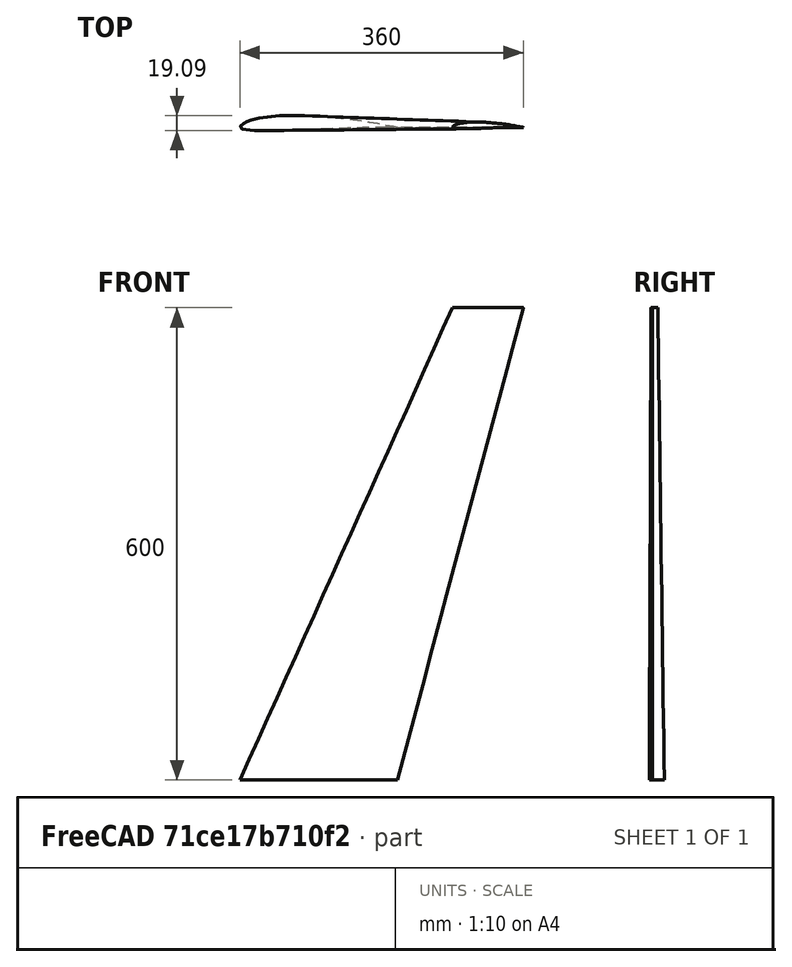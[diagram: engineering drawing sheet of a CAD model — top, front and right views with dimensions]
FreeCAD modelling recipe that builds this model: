
FCSTD DOCUMENT  (FreeCAD 1.0R39109 (Git))
Label: SD7037 Airfoil Wing 160cm Wingspan
License: All rights reserved
LicenseURL: https://en.wikipedia.org/wiki/All_rights_reserved
objects: Part::Part2DObjectPython×4, Sketcher::SketchObject×4, App::DocumentObjectGroup×1, PartDesign::AdditiveLoft×1, PartDesign::Body×1
note: 16 computed .brp shape members not serialized (recipe doc carries the construction recipe); baked Part::Feature solids carry a one-line shape summary decoded from their .brp

FEATURE [Part::Part2DObjectPython] Wire  # Draft 2D object (typed FeaturePython)
  Area = 0.0605284
  ChamferSize = 0
  Closed = true
  End = (1,0,0)
  FilletRadius = 0
  Length = 2.02979
  MakeFace = true
  Points = (61) [(1,0,0),(0.99672,0.00042,0),(0.98707,0.0018,0),(0.97146,0.00436,0),(0.95041,0.00811,0),(0.9245,0.01295,0),(0.89425,0.01865,0),(0.86015,0.0249,0),+53 more]
  Start = (1,0,0)
  Subdivisions = 0
FEATURE [App::DocumentObjectGroup] sd7037
  Group = -> [Wire]
FEATURE [Part::Part2DObjectPython] BSpline  label="SD7037 20CM Length"  # Draft 2D object (typed FeaturePython)
  Area = 2428.78
  Closed = true
  MakeFace = true
  Parameterization = 1
  Points = (60) [(200,0,0),(199.344,0.084,0),(197.414,0.36,0),(194.292,0.872,0),(190.082,1.622,0),(184.9,2.59,0),(178.85,3.73,0),(172.03,4.98,0),(164.522,6.282,0),+51 more]
FEATURE [Part::Part2DObjectPython] BSpline001  label="Original SD7038"  # Draft 2D object (typed FeaturePython)
  Area = 0.0607194
  Closed = true
  MakeFace = true
  Parameterization = 1
  Points = (60) [(1,0,0),(0.99672,0.00042,0),(0.98707,0.0018,0),(0.97146,0.00436,0),(0.95041,0.00811,0),(0.9245,0.01295,0),(0.89425,0.01865,0),(0.86015,0.0249,0),+52 more]
FEATURE [Part::Part2DObjectPython] BSpline002  label="SD7039 9CM Length"  # Draft 2D object (typed FeaturePython)
  Area = 491.827
  Closed = true
  MakeFace = true
  Parameterization = 1
  Points = (60) [(90,0,0),(89.7048,0.0378,0),(88.8363,0.162,0),(87.4314,0.3924,0),(85.5369,0.7299,0),(83.205,1.1655,0),(80.4825,1.6785,0),(77.4135,2.241,0),+52 more]
FEATURE [Sketcher::SketchObject] Sketch
  ArcFitTolerance = 1e-06
  FullyConstrained = false
  MakeInternals = false
  sketch-geometry (123):
    g0: BSplineCurve PolesCount=61 KnotsCount=61 Degree=3 IsPeriodic=1
    g1-g61: Circle [constr] x61 (B-spline internal-alignment scaffolding for g0; pole/knot coordinates omitted)
    g62-g122: GeomPoint [constr] x61 (B-spline internal-alignment scaffolding for g0; pole/knot coordinates omitted)
  constraints (123):
    c: InternalAlignment(g1,g0)
    c: Weight(g1) = 1
    c: InternalAlignment(g2,g0)
    c: Equal(g2,g1)
    c: InternalAlignment(g3,g0)
    c: Equal(g3,g1)
    c: InternalAlignment(g4,g0)
    c: Equal(g4,g1)
    c: InternalAlignment(g5,g0)
    c: Equal(g5,g1)
    c: InternalAlignment(g6,g0)
    c: Equal(g6,g1)
    c: InternalAlignment(g7,g0)
    c: Equal(g7,g1)
    c: InternalAlignment(g8,g0)
    c: Equal(g8,g1)
    c: InternalAlignment(g9,g0)
    c: Equal(g9,g1)
    c: InternalAlignment(g10,g0)
    c: Equal(g10,g1)
    c: InternalAlignment(g11,g0)
    c: Equal(g11,g1)
    c: InternalAlignment(g12,g0)
    c: Equal(g12,g1)
    c: InternalAlignment(g13,g0)
    c: Equal(g13,g1)
    c: InternalAlignment(g14,g0)
    c: Equal(g14,g1)
    c: InternalAlignment(g15,g0)
    c: Equal(g15,g1)
    c: InternalAlignment(g16,g0)
    c: Equal(g16,g1)
    c: InternalAlignment(g17,g0)
    c: Equal(g17,g1)
    c: InternalAlignment(g18,g0)
    c: Equal(g18,g1)
    c: InternalAlignment(g19,g0)
    c: Equal(g19,g1)
    c: InternalAlignment(g20,g0)
    c: Equal(g20,g1)
    c: InternalAlignment(g21,g0)
    c: Equal(g21,g1)
    c: InternalAlignment(g22,g0)
    c: Equal(g22,g1)
    c: InternalAlignment(g23,g0)
    c: Equal(g23,g1)
    c: InternalAlignment(g24,g0)
    c: Equal(g24,g1)
    c: InternalAlignment(g25,g0)
    c: Equal(g25,g1)
    c: InternalAlignment(g26,g0)
    c: Equal(g26,g1)
    c: InternalAlignment(g27,g0)
    c: Equal(g27,g1)
    c: InternalAlignment(g28,g0)
    c: Equal(g28,g1)
    c: InternalAlignment(g29,g0)
    c: Equal(g29,g1)
    c: InternalAlignment(g30,g0)
    c: Equal(g30,g1)
    c: InternalAlignment(g31,g0)
    c: Equal(g31,g1)
    c: InternalAlignment(g32,g0)
    c: Equal(g32,g1)
    c: InternalAlignment(g33,g0)
    c: Equal(g33,g1)
    c: InternalAlignment(g34,g0)
    c: Equal(g34,g1)
    c: InternalAlignment(g35,g0)
    c: Equal(g35,g1)
    c: InternalAlignment(g36,g0)
    c: Equal(g36,g1)
    c: InternalAlignment(g37,g0)
    c: Equal(g37,g1)
    c: InternalAlignment(g38,g0)
    c: Equal(g38,g1)
    c: InternalAlignment(g39,g0)
    c: Equal(g39,g1)
    c: InternalAlignment(g40,g0)
    c: Equal(g40,g1)
    c: InternalAlignment(g41,g0)
    c: Equal(g41,g1)
    c: InternalAlignment(g42,g0)
    c: Equal(g42,g1)
    c: InternalAlignment(g43,g0)
    c: Equal(g43,g1)
    c: InternalAlignment(g44,g0)
    c: Equal(g44,g1)
    c: InternalAlignment(g45,g0)
    c: Equal(g45,g1)
    c: InternalAlignment(g46,g0)
    c: Equal(g46,g1)
    c: InternalAlignment(g47,g0)
    c: Equal(g47,g1)
    c: InternalAlignment(g48,g0)
    c: Equal(g48,g1)
    c: InternalAlignment(g49,g0)
    c: Equal(g49,g1)
    c: InternalAlignment(g50,g0)
    c: Equal(g50,g1)
    c: InternalAlignment(g51,g0)
    c: Equal(g51,g1)
    c: InternalAlignment(g52,g0)
    c: Equal(g52,g1)
    c: InternalAlignment(g53,g0)
    c: Equal(g53,g1)
    c: InternalAlignment(g54,g0)
    c: Equal(g54,g1)
    c: InternalAlignment(g55,g0)
    c: Equal(g55,g1)
    c: InternalAlignment(g56,g0)
    c: Equal(g56,g1)
    c: InternalAlignment(g57,g0)
    c: Equal(g57,g1)
    c: InternalAlignment(g58,g0)
    c: Equal(g58,g1)
    c: InternalAlignment(g59,g0)
    c: Equal(g59,g1)
    c: InternalAlignment(g60,g0)
    c: Equal(g60,g1)
    c: InternalAlignment(g61,g0)
    c: Equal(g61,g1)
    c: InternalAlignment(g62-g122 -> g0) x61
FEATURE [Sketcher::SketchObject] Sketch001
  ArcFitTolerance = 1e-06
  FullyConstrained = false
  MakeInternals = false
  Placement = pos=(270,0,600) rot=(0,0,1;0rad)
  sketch-geometry (123):
    g0: BSplineCurve PolesCount=61 KnotsCount=61 Degree=3 IsPeriodic=1
    g1-g61: Circle [constr] x61 (B-spline internal-alignment scaffolding for g0; pole/knot coordinates omitted)
    g62-g122: GeomPoint [constr] x61 (B-spline internal-alignment scaffolding for g0; pole/knot coordinates omitted)
  constraints (123):
    c: InternalAlignment(g1,g0)
    c: Weight(g1) = 1
    c: InternalAlignment(g2,g0)
    c: Equal(g2,g1)
    c: InternalAlignment(g3,g0)
    c: Equal(g3,g1)
    c: InternalAlignment(g4,g0)
    c: Equal(g4,g1)
    c: InternalAlignment(g5,g0)
    c: Equal(g5,g1)
    c: InternalAlignment(g6,g0)
    c: Equal(g6,g1)
    c: InternalAlignment(g7,g0)
    c: Equal(g7,g1)
    c: InternalAlignment(g8,g0)
    c: Equal(g8,g1)
    c: InternalAlignment(g9,g0)
    c: Equal(g9,g1)
    c: InternalAlignment(g10,g0)
    c: Equal(g10,g1)
    c: InternalAlignment(g11,g0)
    c: Equal(g11,g1)
    c: InternalAlignment(g12,g0)
    c: Equal(g12,g1)
    c: InternalAlignment(g13,g0)
    c: Equal(g13,g1)
    c: InternalAlignment(g14,g0)
    c: Equal(g14,g1)
    c: InternalAlignment(g15,g0)
    c: Equal(g15,g1)
    c: InternalAlignment(g16,g0)
    c: Equal(g16,g1)
    c: InternalAlignment(g17,g0)
    c: Equal(g17,g1)
    c: InternalAlignment(g18,g0)
    c: Equal(g18,g1)
    c: InternalAlignment(g19,g0)
    c: Equal(g19,g1)
    c: InternalAlignment(g20,g0)
    c: Equal(g20,g1)
    c: InternalAlignment(g21,g0)
    c: Equal(g21,g1)
    c: InternalAlignment(g22,g0)
    c: Equal(g22,g1)
    c: InternalAlignment(g23,g0)
    c: Equal(g23,g1)
    c: InternalAlignment(g24,g0)
    c: Equal(g24,g1)
    c: InternalAlignment(g25,g0)
    c: Equal(g25,g1)
    c: InternalAlignment(g26,g0)
    c: Equal(g26,g1)
    c: InternalAlignment(g27,g0)
    c: Equal(g27,g1)
    c: InternalAlignment(g28,g0)
    c: Equal(g28,g1)
    c: InternalAlignment(g29,g0)
    c: Equal(g29,g1)
    c: InternalAlignment(g30,g0)
    c: Equal(g30,g1)
    c: InternalAlignment(g31,g0)
    c: Equal(g31,g1)
    c: InternalAlignment(g32,g0)
    c: Equal(g32,g1)
    c: InternalAlignment(g33,g0)
    c: Equal(g33,g1)
    c: InternalAlignment(g34,g0)
    c: Equal(g34,g1)
    c: InternalAlignment(g35,g0)
    c: Equal(g35,g1)
    c: InternalAlignment(g36,g0)
    c: Equal(g36,g1)
    c: InternalAlignment(g37,g0)
    c: Equal(g37,g1)
    c: InternalAlignment(g38,g0)
    c: Equal(g38,g1)
    c: InternalAlignment(g39,g0)
    c: Equal(g39,g1)
    c: InternalAlignment(g40,g0)
    c: Equal(g40,g1)
    c: InternalAlignment(g41,g0)
    c: Equal(g41,g1)
    c: InternalAlignment(g42,g0)
    c: Equal(g42,g1)
    c: InternalAlignment(g43,g0)
    c: Equal(g43,g1)
    c: InternalAlignment(g44,g0)
    c: Equal(g44,g1)
    c: InternalAlignment(g45,g0)
    c: Equal(g45,g1)
    c: InternalAlignment(g46,g0)
    c: Equal(g46,g1)
    c: InternalAlignment(g47,g0)
    c: Equal(g47,g1)
    c: InternalAlignment(g48,g0)
    c: Equal(g48,g1)
    c: InternalAlignment(g49,g0)
    c: Equal(g49,g1)
    c: InternalAlignment(g50,g0)
    c: Equal(g50,g1)
    c: InternalAlignment(g51,g0)
    c: Equal(g51,g1)
    c: InternalAlignment(g52,g0)
    c: Equal(g52,g1)
    c: InternalAlignment(g53,g0)
    c: Equal(g53,g1)
    c: InternalAlignment(g54,g0)
    c: Equal(g54,g1)
    c: InternalAlignment(g55,g0)
    c: Equal(g55,g1)
    c: InternalAlignment(g56,g0)
    c: Equal(g56,g1)
    c: InternalAlignment(g57,g0)
    c: Equal(g57,g1)
    c: InternalAlignment(g58,g0)
    c: Equal(g58,g1)
    c: InternalAlignment(g59,g0)
    c: Equal(g59,g1)
    c: InternalAlignment(g60,g0)
    c: Equal(g60,g1)
    c: InternalAlignment(g61,g0)
    c: Equal(g61,g1)
    c: InternalAlignment(g62-g122 -> g0) x61
FEATURE [PartDesign::AdditiveLoft] AdditiveLoft
  Closed = false
  Profile = -> Sketch
  Refine = true
  Ruled = false
  Sections = -> [Sketch001]
  Suppressed = false
FEATURE [Sketcher::SketchObject] Sketch002
  ArcFitTolerance = 1e-06
  AttachmentOffset = pos=(0,0,7) rot=(0,0,1;0rad)
  AttachmentSupport = -> [XZ_Plane]
  FullyConstrained = true
  MakeInternals = false
  MapMode = 5
  Placement = pos=(0,-7,1.6e-15) rot=(1,0,0;1.5708rad)
  sketch-geometry (24):
    g0: LineSegment StartX=0 StartY=20 StartZ=0 EndX=300 EndY=20 EndZ=0
    g1: LineSegment StartX=300 StartY=20 StartZ=0 EndX=300 EndY=120 EndZ=0
    g2: LineSegment StartX=300 StartY=120 StartZ=0 EndX=0 EndY=120 EndZ=0
    g3: LineSegment StartX=0 StartY=120 StartZ=0 EndX=0 EndY=20 EndZ=0
    g4: LineSegment StartX=0 StartY=125 StartZ=0 EndX=300 EndY=125 EndZ=0
    g5: LineSegment StartX=300 StartY=125 StartZ=0 EndX=300 EndY=225 EndZ=0
    g6: LineSegment StartX=300 StartY=225 StartZ=0 EndX=0 EndY=225 EndZ=0
    g7: LineSegment StartX=0 StartY=225 StartZ=0 EndX=0 EndY=125 EndZ=0
    g8: LineSegment StartX=0 StartY=230 StartZ=0 EndX=500 EndY=230 EndZ=0
    g9: LineSegment StartX=500 StartY=230 StartZ=0 EndX=500 EndY=330 EndZ=0
    g10: LineSegment StartX=500 StartY=330 StartZ=0 EndX=0 EndY=330 EndZ=0
    g11: LineSegment StartX=0 StartY=335 StartZ=0 EndX=500 EndY=335 EndZ=0
    g12: LineSegment StartX=500 StartY=335 StartZ=0 EndX=500 EndY=435 EndZ=0
    g13: LineSegment StartX=500 StartY=435 StartZ=0 EndX=0 EndY=435 EndZ=0
    g14: LineSegment StartX=0 StartY=435 StartZ=0 EndX=0 EndY=335 EndZ=0
    g15: LineSegment StartX=0 StartY=440 StartZ=0 EndX=500 EndY=440 EndZ=0
    g16: LineSegment StartX=500 StartY=440 StartZ=0 EndX=500 EndY=515 EndZ=0
    g17: LineSegment StartX=500 StartY=515 StartZ=0 EndX=0 EndY=515 EndZ=0
    g18: LineSegment StartX=0 StartY=515 StartZ=0 EndX=0 EndY=440 EndZ=0
    g19: LineSegment StartX=0 StartY=520 StartZ=0 EndX=500 EndY=520 EndZ=0
    g20: LineSegment StartX=500 StartY=520 StartZ=0 EndX=500 EndY=590 EndZ=0
    g21: LineSegment StartX=500 StartY=590 StartZ=0 EndX=0 EndY=590 EndZ=0
    g22: LineSegment StartX=0 StartY=590 StartZ=0 EndX=0 EndY=520 EndZ=0
    g23: LineSegment StartX=0 StartY=330 StartZ=0 EndX=0 EndY=230 EndZ=0
  constraints (72):
    c: Coincident(g0,g1)
    c: Coincident(g1,g2)
    c: Coincident(g2,g3)
    c: Coincident(g3,g0)
    c: Horizontal(g0)
    c: Horizontal(g2)
    c: Vertical(g1)
    c: Vertical(g3)
    c: Coincident(g4,g5)
    c: Coincident(g5,g6)
    c: Coincident(g6,g7)
    c: Coincident(g7,g4)
    c: Horizontal(g4)
    c: Horizontal(g6)
    c: Vertical(g5)
    c: Vertical(g7)
    c: PointOnObject(g4,g-2)
    c: Coincident(g8,g9)
    c: Horizontal(g8)
    c: Horizontal(g10)
    c: Vertical(g9)
    c: PointOnObject(g8,g-2)
    c: PointOnObject(g0,g-2)
    c: Distance(g0,g-1) = 20
    c: DistanceY(g1,g1) = 100
    c: DistanceY(g1,g4) = 5
    c: DistanceY(g5,g5) = 100
    c: DistanceY(g5,g8) = 5
    c: DistanceY(g9,g9) = 100
    c: Coincident(g10,g9)
    c: Coincident(g11,g12)
    c: Coincident(g12,g13)
    c: Coincident(g13,g14)
    c: Coincident(g14,g11)
    c: Horizontal(g11)
    c: Horizontal(g13)
    c: Vertical(g12)
    c: Vertical(g14)
    c: PointOnObject(g11,g-2)
    c: DistanceY(g9,g11) = 5
    c: DistanceY(g12,g12) = 100
    c: Coincident(g15,g16)
    c: Coincident(g16,g17)
    c: Coincident(g17,g18)
    c: Coincident(g18,g15)
    c: Horizontal(g15)
    c: Horizontal(g17)
    c: Vertical(g16)
    c: Vertical(g18)
    c: PointOnObject(g15,g-2)
    c: DistanceY(g12,g15) = 5
    c: DistanceY(g16,g16) = 75
    c: Coincident(g19,g20)
    c: Coincident(g20,g21)
    c: Coincident(g21,g22)
    c: Coincident(g22,g19)
    c: Horizontal(g19)
    c: Horizontal(g21)
    c: Vertical(g20)
    c: Vertical(g22)
    c: PointOnObject(g19,g-2)
    c: DistanceY(g16,g19) = 5
    c: DistanceY(g20,g20) = 70
    c: DistanceX(g0,g0) = 300
    c: DistanceX(g4,g4) = 300
    c: DistanceX(g8,g8) = 500
    c: DistanceX(g11,g11) = 500
    c: DistanceX(g15,g15) = 500
    c: DistanceX(g19,g19) = 500
    c: Coincident(g23,g10)
    c: Coincident(g23,g8)
    c: Vertical(g23)
FEATURE [Sketcher::SketchObject] Sketch003
  ArcFitTolerance = 1e-06
  AttachmentSupport = -> [AdditiveLoft]
  FullyConstrained = false
  MakeInternals = false
  MapMode = 5
  Placement = pos=(0,0,0) rot=(1,0,0;3.14159rad)
  sketch-geometry (39):
    g0: LineSegment StartX=2.86577 StartY=0 StartZ=0 EndX=12.7762 EndY=1.78835 EndZ=0
    g1: LineSegment StartX=12.7762 StartY=1.78835 StartZ=0 EndX=31.141 EndY=2.22365 EndZ=0
    g2: LineSegment StartX=31.141 StartY=2.22365 StartZ=0 EndX=84.2637 EndY=0.856225 EndZ=0
    g3: LineSegment StartX=84.2637 StartY=0.856225 StartZ=0 EndX=135.396 EndY=-1.43302 EndZ=0
    g4: LineSegment StartX=135.396 StartY=-1.43302 StartZ=0 EndX=181.397 EndY=-1.87122 EndZ=0
    g5: LineSegment StartX=2.86577 StartY=0 StartZ=0 EndX=9.58719 EndY=-4.6414 EndZ=0
    g6: LineSegment StartX=9.58719 StartY=-4.6414 StartZ=0 EndX=23.0584 EndY=-8.5721 EndZ=0
    g7: LineSegment StartX=109.104 StartY=-10.6623 StartZ=0 EndX=144.373 EndY=-7.06964 EndZ=0
    g8: LineSegment StartX=144.373 StartY=-7.06964 StartZ=0 EndX=181.397 EndY=-1.87122 EndZ=0
    g9: LineSegment StartX=51.2568 StartY=-12.0449 StartZ=0 EndX=79.1328 EndY=-12.3705 EndZ=0
    g10: LineSegment StartX=79.1328 StartY=-12.3705 StartZ=0 EndX=109.104 EndY=-10.6623 EndZ=0
    g11: LineSegment StartX=23.0584 StartY=-8.5721 StartZ=0 EndX=36.1469 EndY=-10.7538 EndZ=0
    g12: LineSegment StartX=36.1469 StartY=-10.7538 StartZ=0 EndX=51.2568 EndY=-12.0449 EndZ=0
    g13: LineSegment StartX=14.9176 StartY=-6.19672 StartZ=0 EndX=20.2059 EndY=1.96446 EndZ=0
    g14: LineSegment StartX=17.3961 StartY=-6.91992 StartZ=0 EndX=23.1991 EndY=2.0354 EndZ=0
    g15: LineSegment StartX=26.9145 StartY=2.12347 StartZ=0 EndX=31.5791 EndY=-9.99241 EndZ=0
    g16: LineSegment StartX=29.6047 StartY=2.18723 StartZ=0 EndX=34.4799 EndY=-10.476 EndZ=0
    g17: LineSegment StartX=39.1931 StartY=-11.0141 StartZ=0 EndX=46.0177 EndY=1.84071 EndZ=0
    g18: LineSegment StartX=41.9039 StartY=-11.2457 StartZ=0 EndX=48.8133 EndY=1.76875 EndZ=0
    g19: LineSegment StartX=52.257 StartY=1.6801 StartZ=0 EndX=58.4644 EndY=-12.1291 EndZ=0
    g20: LineSegment StartX=57.7023 StartY=1.53994 StartZ=0 EndX=63.8752 EndY=-12.1923 EndZ=0
    g21: LineSegment StartX=65.1948 StartY=-12.2077 StartZ=0 EndX=73.4116 EndY=1.13557 EndZ=0
    g22: LineSegment StartX=71.2282 StartY=-12.2782 StartZ=0 EndX=79.3936 EndY=0.981584 EndZ=0
    g23: LineSegment StartX=80.8648 StartY=0.943715 StartZ=0 EndX=85.6738 EndY=-11.9977 EndZ=0
    g24: LineSegment StartX=85.4821 StartY=0.801674 StartZ=0 EndX=90.1437 EndY=-11.743 EndZ=0
    g25: LineSegment StartX=94.1184 StartY=-11.5164 StartZ=0 EndX=98.7507 EndY=0 EndZ=0
    g26: LineSegment StartX=98.2204 StartY=-11.2826 StartZ=0 EndX=102.77 EndY=0.0276865 EndZ=0
    g27: LineSegment StartX=104.125 StartY=-0.0329787 StartZ=0 EndX=110.253 EndY=-10.5453 EndZ=0
    g28: LineSegment StartX=109.83 StartY=-0.288397 StartZ=0 EndX=115.498 EndY=-10.0111 EndZ=0
    g29: LineSegment StartX=118.802 StartY=-9.67452 StartZ=0 EndX=124.117 EndY=-0.928034 EndZ=0
    g30: LineSegment StartX=123.907 StartY=-9.15442 StartZ=0 EndX=128.78 EndY=-1.13679 EndZ=0
    g31: LineSegment StartX=132.19 StartY=-1.2895 StartZ=0 EndX=137.966 EndY=-7.72232 EndZ=0
    g32: LineSegment StartX=137.313 StartY=-1.45128 StartZ=0 EndX=142.526 EndY=-7.25777 EndZ=0
    g33: LineSegment StartX=146.014 StartY=-6.83926 StartZ=0 EndX=148.65 EndY=-1.55927 EndZ=0
    g34: LineSegment StartX=148.619 StartY=-6.4735 StartZ=0 EndX=151.16 EndY=-1.58319 EndZ=0
    g35: LineSegment StartX=158.396 StartY=-1.65212 StartZ=0 EndX=160.737 EndY=-4.77202 EndZ=0
    g36: LineSegment StartX=161.556 StartY=-1.68222 StartZ=0 EndX=164.867 EndY=-4.19209 EndZ=0
    g37: LineSegment StartX=169.629 StartY=-3.52352 StartZ=0 EndX=170.619 EndY=-1.76855 EndZ=0
    g38: LineSegment StartX=171.706 StartY=-3.23189 StartZ=0 EndX=172.536 EndY=-1.78681 EndZ=0
  constraints (76):
    c: PointOnObject(g0,g-1)
    c: Coincident(g1,g0)
    c: Coincident(g2,g1)
    c: Coincident(g3,g2)
    c: Coincident(g4,g3)
    c: Coincident(g5,g0)
    c: Coincident(g6,g5)
    c: Coincident(g6,g11)
    c: Coincident(g12,g9)
    c: Coincident(g10,g7)
    c: Coincident(g8,g4)
    c: Coincident(g7,g8)
    c: Coincident(g9,g10)
    c: Coincident(g11,g12)
    c: PointOnObject(g13,g6)
    c: PointOnObject(g13,g1)
    c: PointOnObject(g14,g6)
    c: PointOnObject(g14,g1)
    c: PointOnObject(g15,g1)
    c: PointOnObject(g15,g11)
    c: PointOnObject(g16,g1)
    c: PointOnObject(g16,g11)
    c: PointOnObject(g17,g12)
    c: PointOnObject(g17,g2)
    c: PointOnObject(g18,g12)
    c: PointOnObject(g18,g2)
    c: PointOnObject(g19,g2)
    c: PointOnObject(g19,g9)
    c: Symmetric(g2,g2,g20)
    c: PointOnObject(g20,g9)
    c: Symmetric(g9,g9,g21)
    c: PointOnObject(g21,g2)
    c: PointOnObject(g22,g9)
    c: PointOnObject(g22,g2)
    c: PointOnObject(g23,g2)
    c: PointOnObject(g23,g10)
    c: PointOnObject(g24,g3)
    c: PointOnObject(g24,g10)
    c: Symmetric(g10,g10,g25)
    c: PointOnObject(g25,g-1)
    c: PointOnObject(g26,g10)
    c: PointOnObject(g26,g3)
    c: PointOnObject(g27,g3)
    c: PointOnObject(g27,g7)
    c: Symmetric(g3,g3,g28)
    c: PointOnObject(g28,g7)
    c: PointOnObject(g29,g7)
    c: PointOnObject(g29,g3)
    c: PointOnObject(g30,g7)
    c: PointOnObject(g30,g3)
    c: PointOnObject(g31,g3)
    c: PointOnObject(g31,g7)
    c: PointOnObject(g32,g4)
    c: PointOnObject(g32,g7)
    c: PointOnObject(g33,g8)
    c: PointOnObject(g33,g4)
    c: PointOnObject(g34,g8)
    c: PointOnObject(g34,g4)
    c: Symmetric(g4,g4,g35)
    c: PointOnObject(g35,g8)
    c: PointOnObject(g36,g4)
    c: PointOnObject(g36,g8)
    c: PointOnObject(g37,g8)
    c: PointOnObject(g37,g4)
    c: PointOnObject(g38,g8)
    c: PointOnObject(g38,g4)
    c: Parallel(g13,g14)
    c: Parallel(g15,g16)
    c: Parallel(g17,g18)
    c: Parallel(g19,g20)
    c: Parallel(g21,g22)
    c: Parallel(g23,g24)
    c: Parallel(g25,g26)
    c: Parallel(g27,g28)
    c: Parallel(g29,g30)
    c: Parallel(g31,g32)
FEATURE [PartDesign::Body] Body
  AllowCompound = false
  Group = -> [Sketch,Sketch001,AdditiveLoft,Sketch002,Sketch003]
  Origin = -> Origin
  Tip = -> AdditiveLoft
